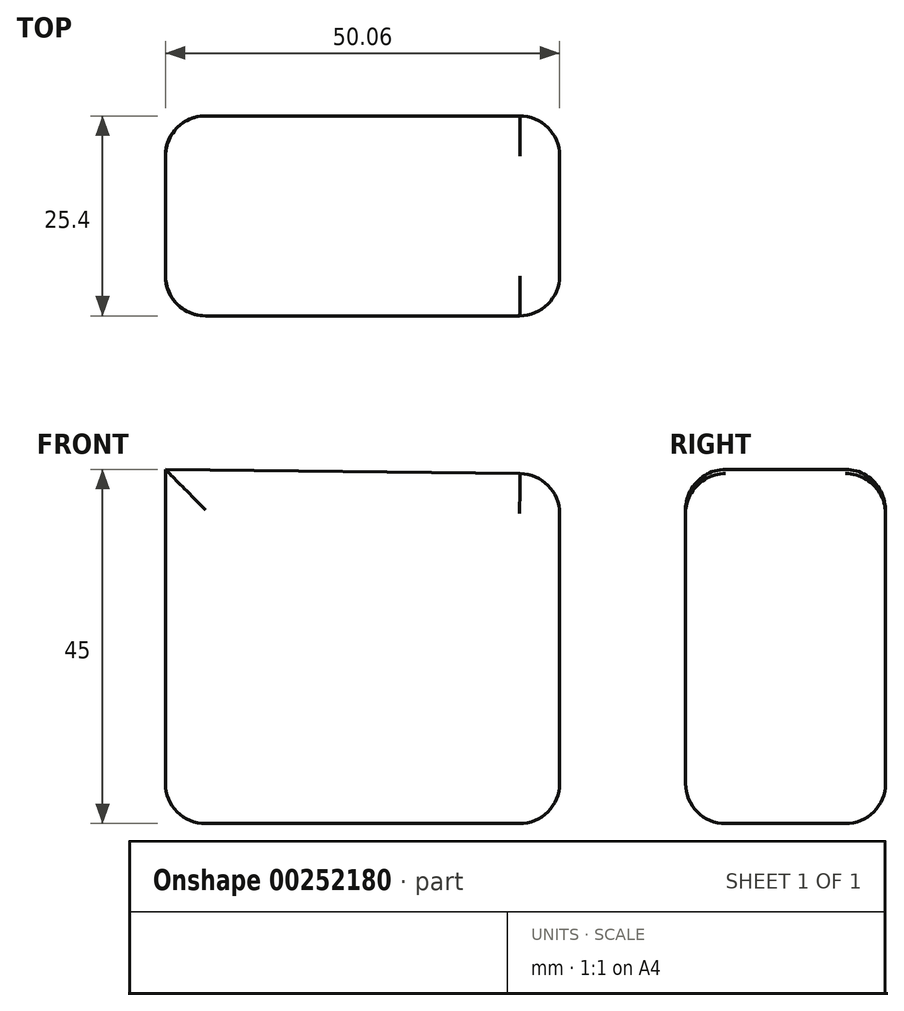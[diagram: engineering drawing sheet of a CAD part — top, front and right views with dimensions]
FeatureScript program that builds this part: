
annotation { "Feature Type Name" : "Feature", "Feature Type Description" : "" }
export const myFeature = defineFeature(function(context is Context, id is Id, definition is map)
    precondition{}
    {
        {
            var Q0;
            Q0=qCreatedBy(makeId("Front.planeOp"),FACE);
            var sketch = newSketch(context, id + "F0", { "sketchPlane" : qUnion([Q0])});
            skLineSegment(sketch, "E0", {"start": v(-58.7, 62.13) * mm, "end": v(-58.7, 17.13) * mm});
            skLineSegment(sketch, "E1", {"start": v(-58.7, 17.13) * mm, "end": v(-8.64, 17.13) * mm});
            skLineSegment(sketch, "E2", {"start": v(-8.64, 17.13) * mm, "end": v(-8.64, 61.53) * mm});
            skLineSegment(sketch, "E3", {"start": v(-8.64, 61.53) * mm, "end": v(-58.7, 62.13) * mm});
            skSolve(sketch);
        }
        {
            var Q0;
            Q0 = qSketchRegion(id + "F0", true);
            extrude(context, id + "F1", {"entities" : qUnion([Q0]), "depth" : 25.4 * mm});
        }
        {
            var Q0;
            Q0=makeQuery(id+"F1.opExtrude","CAP_FACE",FACE,{"disambiguationData":[OSD([sQuery(id+"F0.wireOp",EDGE,"E0"),sQuery(id+"F0.wireOp",EDGE,"E1"),sQuery(id+"F0.wireOp",EDGE,"E2"),sQuery(id+"F0.wireOp",EDGE,"E3")])],"isStart":false});
            var Q1;
            Q1=makeQuery(id+"F1.opExtrude","CAP_FACE",FACE,{"disambiguationData":[OSD([sQuery(id+"F0.wireOp",EDGE,"E0"),sQuery(id+"F0.wireOp",EDGE,"E1"),sQuery(id+"F0.wireOp",EDGE,"E2"),sQuery(id+"F0.wireOp",EDGE,"E3")])],"isStart":true});
            var Q2;
            Q2=makeQuery(id+"F1.opExtrude","CAP_EDGE",EDGE,{"disambiguationData":[OSD([sQuery(id+"F0.wireOp",EDGE,"E1")])],"isStart":false});
            var Q3;
            Q3=makeQuery(id+"F1.opExtrude","SWEPT_FACE",FACE,{"disambiguationData":[OSD([sQuery(id+"F0.wireOp",EDGE,"E1")])]});
            fillet(context, id + "F2", {"entities" : qUnion([Q0, Q1, Q2, Q3]), "radius" : 5.08 * mm, "tangentPropagation" : true, "allowEdgeOverflow" : false});
        }
        {
            var Q0;
            {var subQ0=sQuery(id+"F0.wireOp",EDGE,"E2");Q0=makeQuery(id+"F2.opFillet","BLEND_FACE",FACE,{"disambiguationData":[OSD([subQ0]),TDD([makeQuery(id+"F1.opExtrude","CAP_EDGE",EDGE,{"disambiguationData":[OSD([subQ0])],"isStart":false})])]});}
            fillet(context, id + "F3", {"entities" : qUnion([Q0]), "radius" : 5.08 * mm, "tangentPropagation" : true, "allowEdgeOverflow" : false});
        }
    });
